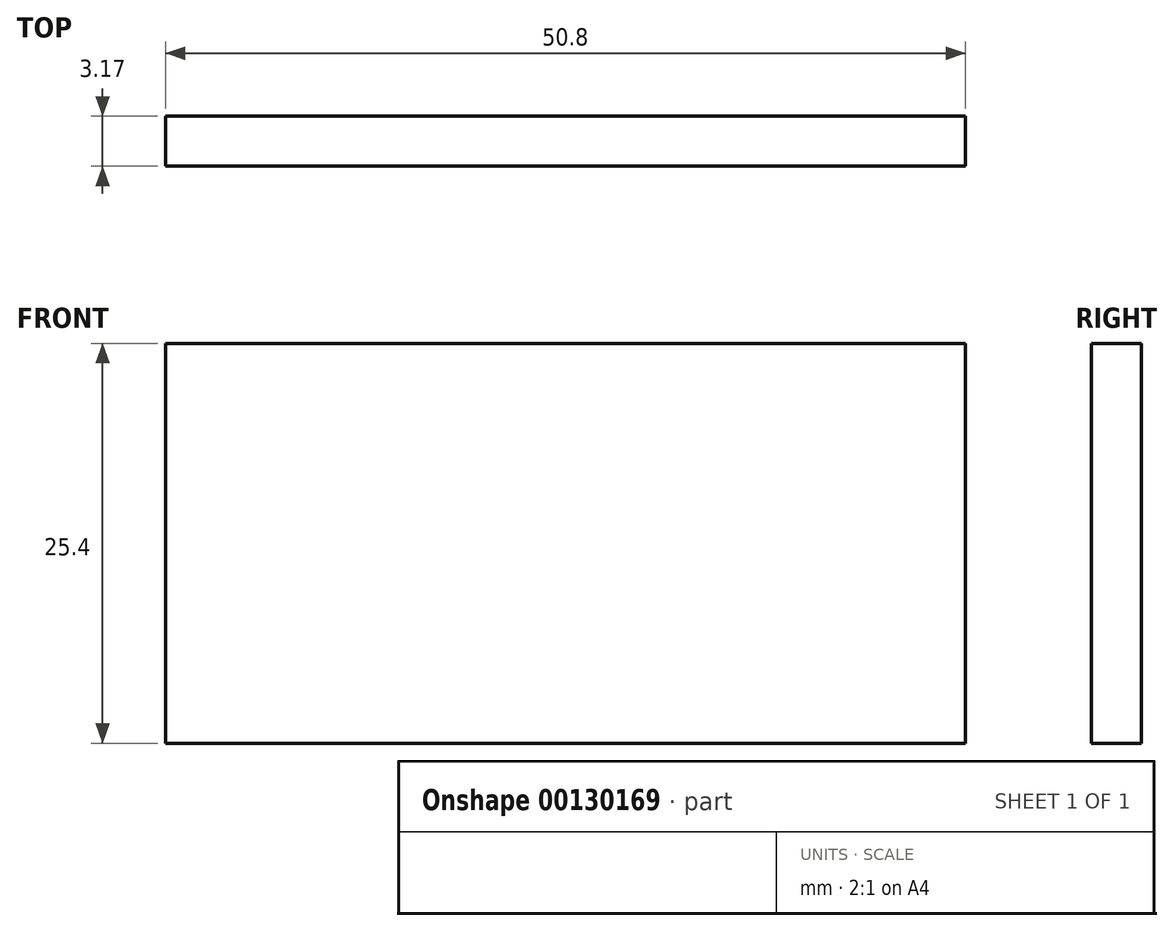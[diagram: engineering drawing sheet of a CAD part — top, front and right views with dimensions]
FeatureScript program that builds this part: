
annotation { "Feature Type Name" : "Feature", "Feature Type Description" : "" }
export const myFeature = defineFeature(function(context is Context, id is Id, definition is map)
    precondition{}
    {
        {
            var Q0;
            Q0=qCreatedBy(makeId("Front.planeOp"),FACE);
            var sketch = newSketch(context, id + "F0", { "sketchPlane" : qUnion([Q0])});
            skLineSegment(sketch, "E0.bottom", {"start": v(-36.27, 34) * mm, "end": v(14.53, 34) * mm});
            skLineSegment(sketch, "E0.top", {"start": v(-36.27, 8.6) * mm, "end": v(14.53, 8.6) * mm});
            skLineSegment(sketch, "E0.left", {"start": v(-36.27, 34) * mm, "end": v(-36.27, 8.6) * mm});
            skLineSegment(sketch, "E0.right", {"start": v(14.53, 34) * mm, "end": v(14.53, 8.6) * mm});
            skSolve(sketch);
        }
        {
            var Q0;
            Q0=makeQuery(id+"F0.imprint","IMPRINT",FACE,{"disambiguationData":[TD([[makeQuery(id+"F0.imprint","IMPRINT",EDGE,{"derivedFrom":sQuery(id+"F0.wireOp",EDGE,"E0.bottom")}),-1.0]])]});
            extrude(context, id + "F1", {"entities" : qUnion([Q0]), "depth" : 3.17 * mm});
        }
    });
